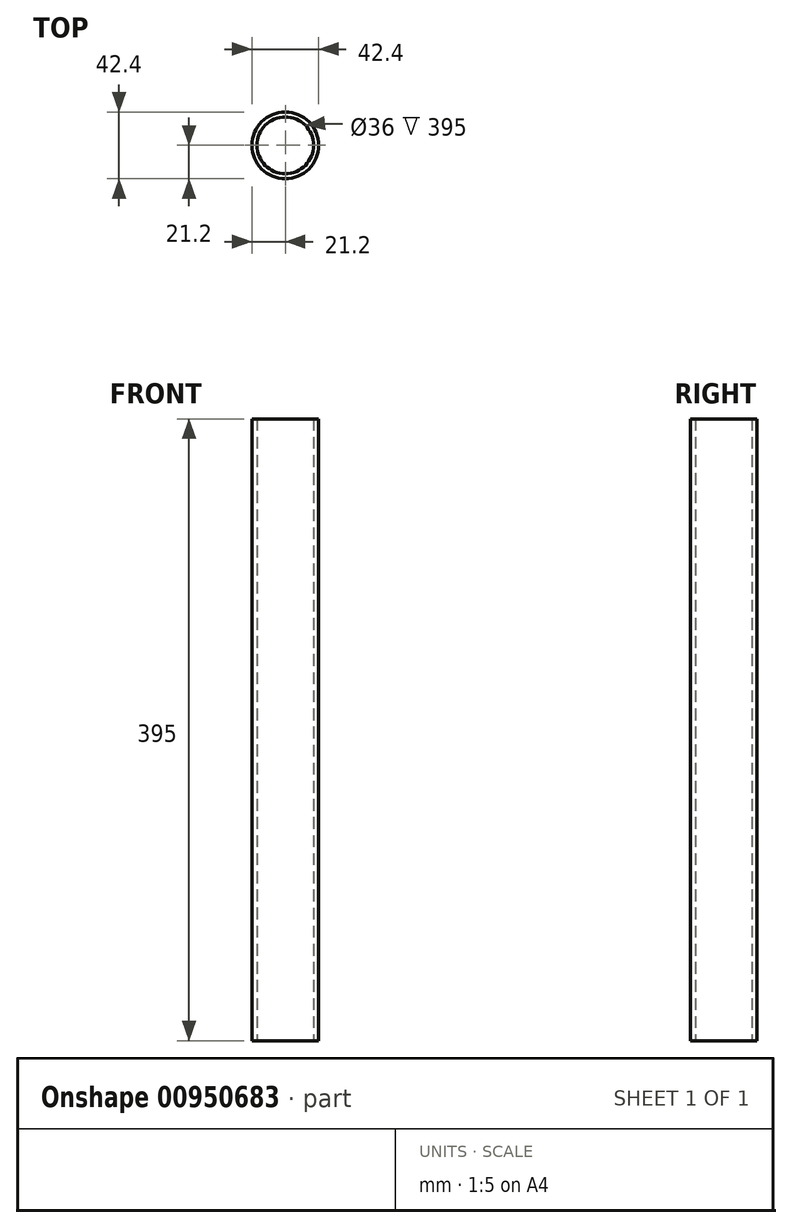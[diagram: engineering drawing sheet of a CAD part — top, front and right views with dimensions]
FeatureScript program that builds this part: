
annotation { "Feature Type Name" : "Feature", "Feature Type Description" : "" }
export const myFeature = defineFeature(function(context is Context, id is Id, definition is map)
    precondition{}
    {
        {
            var Q0;
            Q0=qCreatedBy(makeId("Top.planeOp"),FACE);
            var sketch = newSketch(context, id + "F0", { "sketchPlane" : qUnion([Q0])});
            skCircle(sketch, "E0", {"center": v(0, 0) * mm, "radius": 21.2 * mm});
            skCircle(sketch, "E1.0", {"center": v(0, 0) * mm, "radius": 18 * mm});
            skSolve(sketch);
        }
        {
            var Q0;
            Q0=makeQuery(id+"F0.imprint","IMPRINT",FACE,{"disambiguationData":[TD([[makeQuery(id+"F0.imprint","IMPRINT",EDGE,{"derivedFrom":sQuery(id+"F0.wireOp",EDGE,"E0")}),1.0]])]});
            extrude(context, id + "F1", {"entities" : qUnion([Q0]), "depth" : 395 * mm, "offsetDistance" : 25 * mm});
        }
    });
